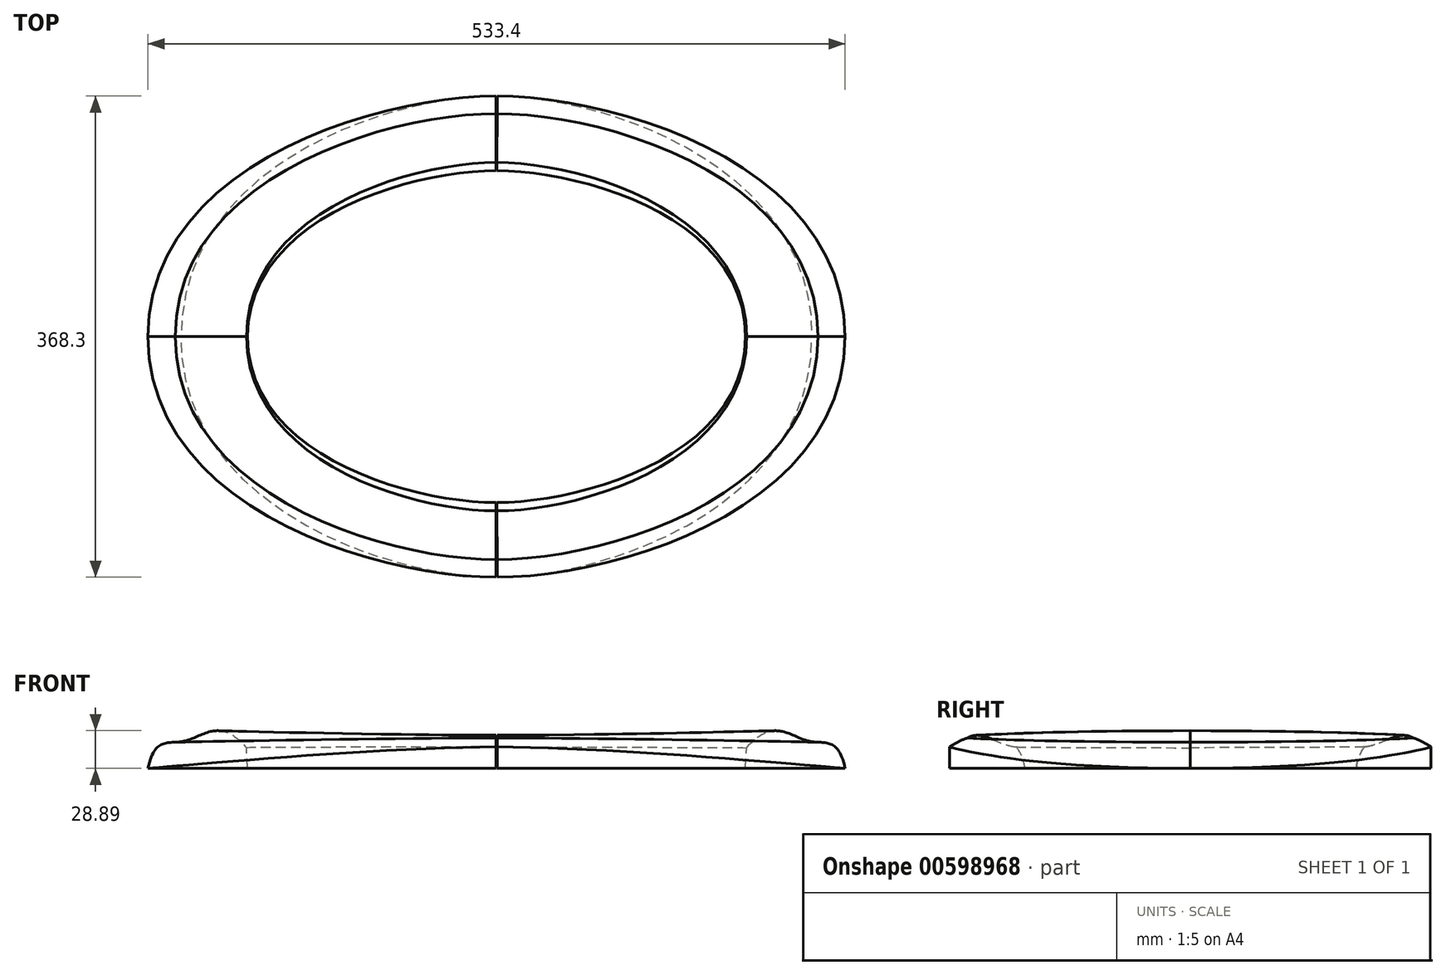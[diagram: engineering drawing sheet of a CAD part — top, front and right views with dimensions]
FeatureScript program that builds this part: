
annotation { "Feature Type Name" : "Feature", "Feature Type Description" : "" }
export const myFeature = defineFeature(function(context is Context, id is Id, definition is map)
    precondition{}
    {
        {
            var Q0;
            Q0=qCreatedBy(makeId("Top.planeOp"),FACE);
            var sketch = newSketch(context, id + "F0", { "sketchPlane" : qUnion([Q0])});
            skEllipticalArc(sketch, "E0", {});
            skLineSegment(sketch, "E1", {"start": v(-0.13, 0) * mm, "end": v(0, 0) * mm});
            skPoint(sketch, "E2.end.orphan", {"position": v(0, -127) * mm});
            skLineSegment(sketch, "E3", {"start": v(-0.37, 127) * mm, "end": v(0, 127) * mm});
            skEllipticalArc(sketch, "E4", {});
            const initialGuessF0  = {"E0": [0, 0, 1, 0, 0.1905, 0.127, 1.5727613835247567, 3.141592653589793], "E4": [0, 0, 1, 0, 0.1905, 0.127, 3.141592653589793, 1.5707963267948966]};
            skSetInitialGuess(sketch, initialGuessF0);
            skSolve(sketch);
        }
        {
            var Q0;
            Q0=sQuery(id+"F0.wireOp",EDGE,"E0");
            var Q1;
            Q1=sQuery(id+"F0.wireOp",VERTEX,"E0.start");
            cPlane(context, id + "F1", {"entities" : qUnion([Q0, Q1]), "cplaneType" : CPlaneType.CURVE_POINT, "offset" : 25.4 * mm, "width" : 152.4 * mm, "height" : 152.4 * mm});
        }
        {
            var Q0;
            Q0=qCreatedBy(id+"F1.planeOp",FACE);
            var sketch = newSketch(context, id + "F2", { "sketchPlane" : qUnion([Q0])});
            skLineSegment(sketch, "E5", {"start": v(-127, 0) * mm, "end": v(-184.15, 0) * mm});
            skLineSegment(sketch, "E6", {"start": v(-184.15, 0) * mm, "end": v(-184.15, 16.51) * mm});
            skArc(sketch, "E7", {"start": v(-170.7, 23.37) * mm, "mid": v(-177.67, 20.41) * mm, "end": v(-184.15, 16.51) * mm});
            skArc(sketch, "E8", {"start": v(-127, 0) * mm, "mid": v(-128.88, 8.75) * mm, "end": v(-133.35, 16.51) * mm});
            skFitSpline(sketch, "E9", {"points": [v(-133.35, 16.51) * mm, v(-170.7, 23.37) * mm], "startDerivative": vector(-45.64, 4.98) * mm, "endDerivative": vector(-35.41, -20.13) * mm});
            skLineSegment(sketch, "E10", {"start": v(-163.32, 0) * mm, "end": v(-163.32, 25.4) * mm});
            skSolve(sketch);
        }
        {
            var Q0;
            Q0=qCreatedBy(makeId("Front.planeOp"),FACE);
            var sketch = newSketch(context, id + "F3", { "sketchPlane" : qUnion([Q0])});
            skLineSegment(sketch, "E11", {"start": v(-266.7, 0) * mm, "end": v(-190.5, 0) * mm});
            skLineSegment(sketch, "E12", {"start": v(-190.5, 0) * mm, "end": v(-191.33, 15.85) * mm});
            skFitSpline(sketch, "E13", {"points": [v(-266.7, 0) * mm, v(-238.76, 20.96) * mm, v(-191.33, 15.85) * mm], "startDerivative": vector(33.76, 162.28) * mm, "endDerivative": vector(110.83, -133.2) * mm});
            skFitSpline(sketch, "E14", {"points": [v(-266.7, 0) * mm, v(-238.76, 20.96) * mm, v(-191.33, 15.85) * mm], "startDerivative": vector(33.76, 162.28) * mm, "endDerivative": vector(110.83, -133.2) * mm});
            skLineSegment(sketch, "E15", {"start": v(-215.93, 0) * mm, "end": v(-217.43, 28.54) * mm});
            skSolve(sketch);
        }
        {
            var Q0;
            Q0=qSketchRegion(id+"F2",true);
            var Q1;
            Q1=qSketchRegion(id+"F3",true);
            loft(context, id + "F4", {"startCondition" : LoftEndDerivativeType.NORMAL_TO_PROFILE, "startMagnitude" : 1, "endCondition" : LoftEndDerivativeType.NORMAL_TO_PROFILE, "endMagnitude" : 2, "sheetProfilesArray" : [{ "sheetProfileEntities" : qUnion([Q0]) }, { "sheetProfileEntities" : qUnion([Q1]) }]});
        }
        {
            var Q0;
            Q0=makeQuery(id+"F4.opLoft","SWEPT_BODY",BODY,{"disambiguationData":[OSD([makeQuery(id+"F2.imprint","IMPRINT",FACE,{"disambiguationData":[TD([[makeQuery(id+"F2.imprint","IMPRINT",EDGE,{"derivedFrom":sQuery(id+"F2.wireOp",EDGE,"E5")}),-1.0]])]}),makeQuery(id+"F3.imprint","IMPRINT",FACE,{"disambiguationData":[TD([[makeQuery(id+"F3.imprint","IMPRINT",EDGE,{"derivedFrom":sQuery(id+"F3.wireOp",EDGE,"E11")}),1.0]])]})])]});
            var Q1;
            Q1=qCreatedBy(makeId("Right.planeOp"),FACE);
            mirror(context, id + "F5", {"entities" : qUnion([Q0]), "mirrorPlane" : qUnion([Q1])});
        }
        {
            var Q0;
            Q0=makeQuery(id+"F4.opLoft","SWEPT_BODY",BODY,{"disambiguationData":[OSD([makeQuery(id+"F2.imprint","IMPRINT",FACE,{"disambiguationData":[TD([[makeQuery(id+"F2.imprint","IMPRINT",EDGE,{"derivedFrom":sQuery(id+"F2.wireOp",EDGE,"E5")}),-1.0]])]}),makeQuery(id+"F3.imprint","IMPRINT",FACE,{"disambiguationData":[TD([[makeQuery(id+"F3.imprint","IMPRINT",EDGE,{"derivedFrom":sQuery(id+"F3.wireOp",EDGE,"E11")}),1.0]])]})])]});
            var Q1;
            Q1=makeQuery(id+"F5.opPattern","COPY",BODY,{"derivedFrom":makeQuery(id+"F4.opLoft","SWEPT_BODY",BODY,{"disambiguationData":[OSD([makeQuery(id+"F2.imprint","IMPRINT",FACE,{"disambiguationData":[TD([[makeQuery(id+"F2.imprint","IMPRINT",EDGE,{"derivedFrom":sQuery(id+"F2.wireOp",EDGE,"E5")}),-1.0]])]}),makeQuery(id+"F3.imprint","IMPRINT",FACE,{"disambiguationData":[TD([[makeQuery(id+"F3.imprint","IMPRINT",EDGE,{"derivedFrom":sQuery(id+"F3.wireOp",EDGE,"E11")}),1.0]])]})])]}),"instanceName":"1"});
            var Q2;
            Q2=qCreatedBy(makeId("Front.planeOp"),FACE);
            mirror(context, id + "F6", {"entities" : qUnion([Q0, Q1]), "mirrorPlane" : qUnion([Q2])});
        }
    });
